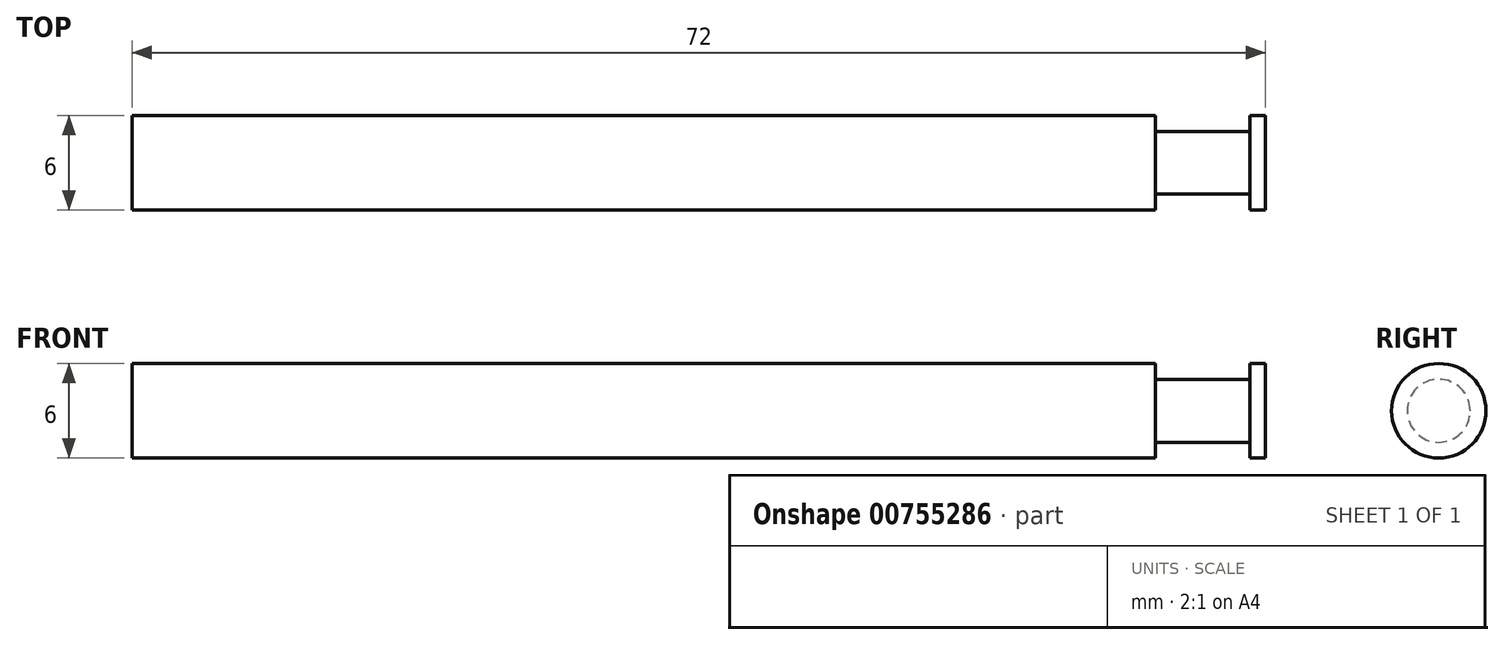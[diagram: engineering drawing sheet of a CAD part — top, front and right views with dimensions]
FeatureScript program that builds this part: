
annotation { "Feature Type Name" : "Feature", "Feature Type Description" : "" }
export const myFeature = defineFeature(function(context is Context, id is Id, definition is map)
    precondition{}
    {
        {
            var Q0;
            Q0=qCreatedBy(makeId("Right.planeOp"),FACE);
            var sketch = newSketch(context, id + "F0", { "sketchPlane" : qUnion([Q0])});
            skCircle(sketch, "E0", {"center": v(0, 0) * mm, "radius": 3 * mm});
            skSolve(sketch);
        }
        {
            var Q0;
            Q0=makeQuery(id+"F0.imprint","IMPRINT",FACE,{"disambiguationData":[TD([[makeQuery(id+"F0.imprint","IMPRINT",EDGE,{"derivedFrom":sQuery(id+"F0.wireOp",EDGE,"E0")}),1.0]])]});
            extrude(context, id + "F1", {"entities" : qUnion([Q0]), "depth" : 65 * mm, "offsetDistance" : 25 * mm});
        }
        {
            var Q0;
            Q0=makeQuery(id+"F1.opExtrude","CAP_FACE",FACE,{"disambiguationData":[OSD([sQuery(id+"F0.wireOp",EDGE,"E0")])],"isStart":false});
            var sketch = newSketch(context, id + "F2", { "sketchPlane" : qUnion([Q0])});
            skCircle(sketch, "E1", {"center": v(0, 0) * mm, "radius": 2 * mm});
            skSolve(sketch);
        }
        {
            var Q0;
            Q0=makeQuery(id+"F2.imprint","IMPRINT",FACE,{"disambiguationData":[TD([[makeQuery(id+"F2.imprint","IMPRINT",EDGE,{"derivedFrom":sQuery(id+"F2.wireOp",EDGE,"E1")}),1.0]])]});
            extrude(context, id + "F3", {"entities" : qUnion([Q0]), "operationType" : NewBodyOperationType.ADD, "depth" : 6 * mm, "offsetDistance" : 25 * mm});
        }
        {
            var Q0;
            Q0=makeQuery(id+"F3.opExtrude","CAP_FACE",FACE,{"disambiguationData":[OSD([sQuery(id+"F2.wireOp",EDGE,"E1")])],"isStart":false});
            var sketch = newSketch(context, id + "F4", { "sketchPlane" : qUnion([Q0])});
            skCircle(sketch, "E2", {"center": v(0, 0) * mm, "radius": 3 * mm});
            skSolve(sketch);
        }
        {
            var Q0;
            Q0=qSketchRegion(id+"F4",true);
            extrude(context, id + "F5", {"entities" : qUnion([Q0]), "operationType" : NewBodyOperationType.ADD, "depth" : 1 * mm, "offsetDistance" : 25 * mm});
        }
    });
